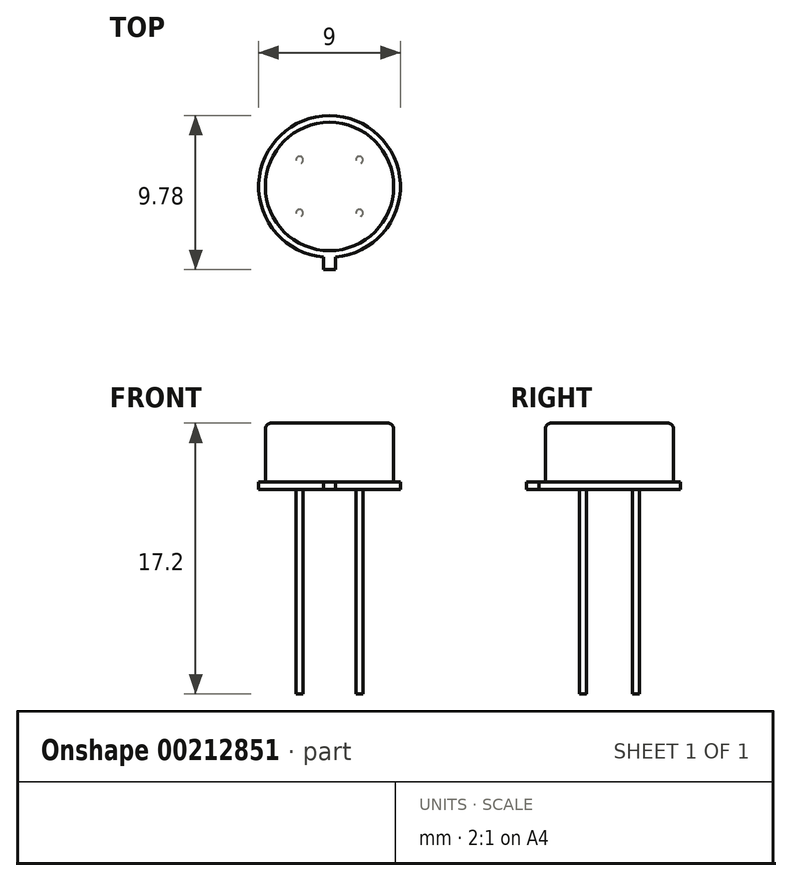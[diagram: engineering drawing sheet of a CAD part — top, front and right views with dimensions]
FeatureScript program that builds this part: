
annotation { "Feature Type Name" : "Feature", "Feature Type Description" : "" }
export const myFeature = defineFeature(function(context is Context, id is Id, definition is map)
    precondition{}
    {
        {
            var Q0;
            Q0=qCreatedBy(makeId("Top.planeOp"),FACE);
            var sketch = newSketch(context, id + "F0", { "sketchPlane" : qUnion([Q0])});
            skCircle(sketch, "E0", {"center": v(0, 0) * mm, "radius": 4.5 * mm});
            skLineSegment(sketch, "E1", {"start": v(-0.37, -4.48) * mm, "end": v(-0.37, -5.28) * mm});
            skLineSegment(sketch, "E2", {"start": v(-0.37, -5.28) * mm, "end": v(0.38, -5.28) * mm});
            skLineSegment(sketch, "E3", {"start": v(0.38, -5.28) * mm, "end": v(0.38, -4.48) * mm});
            skCircle(sketch, "E4", {"center": v(0, 0) * mm, "radius": 2.54 * mm});
            skCircle(sketch, "E5", {"center": v(-1.9, 1.69) * mm, "radius": 0.23 * mm});
            skCircle(sketch, "E6", {"center": v(-1.9, -1.69) * mm, "radius": 0.23 * mm});
            skCircle(sketch, "E7", {"center": v(1.9, -1.69) * mm, "radius": 0.23 * mm});
            skCircle(sketch, "E8", {"center": v(1.9, 1.69) * mm, "radius": 0.23 * mm});
            skCircle(sketch, "E9", {"center": v(0, 0) * mm, "radius": 4.08 * mm});
            skSolve(sketch);
        }
        {
            var Q0;
            Q0=makeQuery(id+"F0.imprint","IMPRINT",FACE,{"disambiguationData":[TD([[makeQuery(id+"F0.imprint","IMPRINT",EDGE,{"derivedFrom":sQuery(id+"F0.wireOp",EDGE,"E9")}),-1.0]])]});
            var Q1;
            {var subQ0=sQuery(id+"F0.wireOp",EDGE,"E1");Q1=makeQuery(id+"F0.imprint","IMPRINT",FACE,{"disambiguationData":[TD([[makeQuery(id+"F0.imprint","IMPRINT",EDGE,{"derivedFrom":subQ0}),1.0]])]});}
            var Q2;
            {var subQ0=sQuery(id+"F0.wireOp",EDGE,"E5");var subQ1=sQuery(id+"F0.wireOp",EDGE,"E4");var subQ2=makeQuery(id+"F0.imprint","INTERSECT",VERTEX,{"disambiguationData":[OD(0.0)],"derivedFrom":[subQ1,subQ0]});Q2=makeQuery(id+"F0.imprint","IMPRINT",FACE,{"disambiguationData":[TD([[makeQuery(id+"F0.imprint","IMPRINT",EDGE,{"disambiguationData":[TD([[subQ2,-1.0]])],"derivedFrom":subQ1}),1.0]])]});}
            var Q3;
            {var subQ0=sQuery(id+"F0.wireOp",EDGE,"E5");var subQ1=sQuery(id+"F0.wireOp",EDGE,"E4");var subQ2=makeQuery(id+"F0.imprint","INTERSECT",VERTEX,{"disambiguationData":[OD(0.0)],"derivedFrom":[subQ1,subQ0]});Q3=makeQuery(id+"F0.imprint","IMPRINT",FACE,{"disambiguationData":[TD([[makeQuery(id+"F0.imprint","IMPRINT",EDGE,{"disambiguationData":[TD([[subQ2,-1.0]])],"derivedFrom":subQ1}),-1.0]])]});}
            var Q4;
            {var subQ0=sQuery(id+"F0.wireOp",EDGE,"E8");var subQ1=sQuery(id+"F0.wireOp",EDGE,"E4");var subQ2=makeQuery(id+"F0.imprint","INTERSECT",VERTEX,{"disambiguationData":[OD(0.0)],"derivedFrom":[subQ1,subQ0]});Q4=makeQuery(id+"F0.imprint","IMPRINT",FACE,{"disambiguationData":[TD([[makeQuery(id+"F0.imprint","IMPRINT",EDGE,{"disambiguationData":[TD([[subQ2,1.0]])],"derivedFrom":subQ1}),-1.0]])]});}
            var Q5;
            {var subQ0=sQuery(id+"F0.wireOp",EDGE,"E8");var subQ1=sQuery(id+"F0.wireOp",EDGE,"E4");var subQ2=makeQuery(id+"F0.imprint","INTERSECT",VERTEX,{"disambiguationData":[OD(0.0)],"derivedFrom":[subQ1,subQ0]});Q5=makeQuery(id+"F0.imprint","IMPRINT",FACE,{"disambiguationData":[TD([[makeQuery(id+"F0.imprint","IMPRINT",EDGE,{"disambiguationData":[TD([[subQ2,1.0]])],"derivedFrom":subQ1}),1.0]])]});}
            var Q6;
            Q6=makeQuery(id+"F0.imprint","IMPRINT",FACE,{"disambiguationData":[TD([[makeQuery(id+"F0.imprint","IMPRINT",EDGE,{"derivedFrom":sQuery(id+"F0.wireOp",EDGE,"E9")}),1.0]])]});
            var Q7;
            {var subQ0=sQuery(id+"F0.wireOp",EDGE,"E7");var subQ1=sQuery(id+"F0.wireOp",EDGE,"E4");var subQ2=makeQuery(id+"F0.imprint","INTERSECT",VERTEX,{"disambiguationData":[OD(0.0)],"derivedFrom":[subQ1,subQ0]});Q7=makeQuery(id+"F0.imprint","IMPRINT",FACE,{"disambiguationData":[TD([[makeQuery(id+"F0.imprint","IMPRINT",EDGE,{"disambiguationData":[TD([[subQ2,-1.0]])],"derivedFrom":subQ1}),1.0]])]});}
            var Q8;
            {var subQ0=sQuery(id+"F0.wireOp",EDGE,"E7");var subQ1=sQuery(id+"F0.wireOp",EDGE,"E4");var subQ2=makeQuery(id+"F0.imprint","INTERSECT",VERTEX,{"disambiguationData":[OD(0.0)],"derivedFrom":[subQ1,subQ0]});Q8=makeQuery(id+"F0.imprint","IMPRINT",FACE,{"disambiguationData":[TD([[makeQuery(id+"F0.imprint","IMPRINT",EDGE,{"disambiguationData":[TD([[subQ2,-1.0]])],"derivedFrom":subQ1}),-1.0]])]});}
            var Q9;
            {var subQ0=sQuery(id+"F0.wireOp",EDGE,"E6");var subQ1=sQuery(id+"F0.wireOp",EDGE,"E4");var subQ2=makeQuery(id+"F0.imprint","INTERSECT",VERTEX,{"disambiguationData":[OD(0.0)],"derivedFrom":[subQ1,subQ0]});Q9=makeQuery(id+"F0.imprint","IMPRINT",FACE,{"disambiguationData":[TD([[makeQuery(id+"F0.imprint","IMPRINT",EDGE,{"disambiguationData":[TD([[subQ2,-1.0]])],"derivedFrom":subQ1}),1.0]])]});}
            var Q10;
            {var subQ0=sQuery(id+"F0.wireOp",EDGE,"E6");var subQ1=sQuery(id+"F0.wireOp",EDGE,"E4");var subQ2=makeQuery(id+"F0.imprint","INTERSECT",VERTEX,{"disambiguationData":[OD(0.0)],"derivedFrom":[subQ1,subQ0]});Q10=makeQuery(id+"F0.imprint","IMPRINT",FACE,{"disambiguationData":[TD([[makeQuery(id+"F0.imprint","IMPRINT",EDGE,{"disambiguationData":[TD([[subQ2,-1.0]])],"derivedFrom":subQ1}),-1.0]])]});}
            var Q11;
            {var subQ0=sQuery(id+"F0.wireOp",EDGE,"E8");var subQ1=sQuery(id+"F0.wireOp",EDGE,"E4");var subQ11=makeQuery(id+"F0.imprint","INTERSECT",VERTEX,{"disambiguationData":[OD(0.0)],"derivedFrom":[subQ1,subQ0]});Q11=makeQuery(id+"F0.imprint","IMPRINT",FACE,{"disambiguationData":[TD([[makeQuery(id+"F0.imprint","IMPRINT",EDGE,{"disambiguationData":[TD([[subQ11,-1.0]])],"derivedFrom":subQ1}),1.0]])]});}
            extrude(context, id + "F1", {"entities" : qUnion([Q0, Q1, Q2, Q3, Q4, Q5, Q6, Q7, Q8, Q9, Q10, Q11]), "depth" : 0.45 * mm});
        }
        {
            var Q0;
            Q0=makeQuery(id+"F0.imprint","IMPRINT",FACE,{"disambiguationData":[TD([[makeQuery(id+"F0.imprint","IMPRINT",EDGE,{"derivedFrom":sQuery(id+"F0.wireOp",EDGE,"E9")}),1.0]])]});
            var Q1;
            {var subQ0=sQuery(id+"F0.wireOp",EDGE,"E8");var subQ1=sQuery(id+"F0.wireOp",EDGE,"E4");var subQ11=makeQuery(id+"F0.imprint","INTERSECT",VERTEX,{"disambiguationData":[OD(0.0)],"derivedFrom":[subQ1,subQ0]});Q1=makeQuery(id+"F0.imprint","IMPRINT",FACE,{"disambiguationData":[TD([[makeQuery(id+"F0.imprint","IMPRINT",EDGE,{"disambiguationData":[TD([[subQ11,-1.0]])],"derivedFrom":subQ1}),1.0]])]});}
            var Q2;
            {var subQ0=sQuery(id+"F0.wireOp",EDGE,"E8");var subQ1=sQuery(id+"F0.wireOp",EDGE,"E4");var subQ2=makeQuery(id+"F0.imprint","INTERSECT",VERTEX,{"disambiguationData":[OD(0.0)],"derivedFrom":[subQ1,subQ0]});Q2=makeQuery(id+"F0.imprint","IMPRINT",FACE,{"disambiguationData":[TD([[makeQuery(id+"F0.imprint","IMPRINT",EDGE,{"disambiguationData":[TD([[subQ2,1.0]])],"derivedFrom":subQ1}),-1.0]])]});}
            var Q3;
            {var subQ0=sQuery(id+"F0.wireOp",EDGE,"E8");var subQ1=sQuery(id+"F0.wireOp",EDGE,"E4");var subQ2=makeQuery(id+"F0.imprint","INTERSECT",VERTEX,{"disambiguationData":[OD(0.0)],"derivedFrom":[subQ1,subQ0]});Q3=makeQuery(id+"F0.imprint","IMPRINT",FACE,{"disambiguationData":[TD([[makeQuery(id+"F0.imprint","IMPRINT",EDGE,{"disambiguationData":[TD([[subQ2,1.0]])],"derivedFrom":subQ1}),1.0]])]});}
            var Q4;
            {var subQ0=sQuery(id+"F0.wireOp",EDGE,"E6");var subQ1=sQuery(id+"F0.wireOp",EDGE,"E4");var subQ2=makeQuery(id+"F0.imprint","INTERSECT",VERTEX,{"disambiguationData":[OD(0.0)],"derivedFrom":[subQ1,subQ0]});Q4=makeQuery(id+"F0.imprint","IMPRINT",FACE,{"disambiguationData":[TD([[makeQuery(id+"F0.imprint","IMPRINT",EDGE,{"disambiguationData":[TD([[subQ2,-1.0]])],"derivedFrom":subQ1}),1.0]])]});}
            var Q5;
            {var subQ0=sQuery(id+"F0.wireOp",EDGE,"E5");var subQ1=sQuery(id+"F0.wireOp",EDGE,"E4");var subQ2=makeQuery(id+"F0.imprint","INTERSECT",VERTEX,{"disambiguationData":[OD(0.0)],"derivedFrom":[subQ1,subQ0]});Q5=makeQuery(id+"F0.imprint","IMPRINT",FACE,{"disambiguationData":[TD([[makeQuery(id+"F0.imprint","IMPRINT",EDGE,{"disambiguationData":[TD([[subQ2,-1.0]])],"derivedFrom":subQ1}),-1.0]])]});}
            var Q6;
            {var subQ0=sQuery(id+"F0.wireOp",EDGE,"E5");var subQ1=sQuery(id+"F0.wireOp",EDGE,"E4");var subQ2=makeQuery(id+"F0.imprint","INTERSECT",VERTEX,{"disambiguationData":[OD(0.0)],"derivedFrom":[subQ1,subQ0]});Q6=makeQuery(id+"F0.imprint","IMPRINT",FACE,{"disambiguationData":[TD([[makeQuery(id+"F0.imprint","IMPRINT",EDGE,{"disambiguationData":[TD([[subQ2,-1.0]])],"derivedFrom":subQ1}),1.0]])]});}
            var Q7;
            {var subQ0=sQuery(id+"F0.wireOp",EDGE,"E7");var subQ1=sQuery(id+"F0.wireOp",EDGE,"E4");var subQ2=makeQuery(id+"F0.imprint","INTERSECT",VERTEX,{"disambiguationData":[OD(0.0)],"derivedFrom":[subQ1,subQ0]});Q7=makeQuery(id+"F0.imprint","IMPRINT",FACE,{"disambiguationData":[TD([[makeQuery(id+"F0.imprint","IMPRINT",EDGE,{"disambiguationData":[TD([[subQ2,-1.0]])],"derivedFrom":subQ1}),-1.0]])]});}
            var Q8;
            {var subQ0=sQuery(id+"F0.wireOp",EDGE,"E7");var subQ1=sQuery(id+"F0.wireOp",EDGE,"E4");var subQ2=makeQuery(id+"F0.imprint","INTERSECT",VERTEX,{"disambiguationData":[OD(0.0)],"derivedFrom":[subQ1,subQ0]});Q8=makeQuery(id+"F0.imprint","IMPRINT",FACE,{"disambiguationData":[TD([[makeQuery(id+"F0.imprint","IMPRINT",EDGE,{"disambiguationData":[TD([[subQ2,-1.0]])],"derivedFrom":subQ1}),1.0]])]});}
            var Q9;
            {var subQ0=sQuery(id+"F0.wireOp",EDGE,"E6");var subQ1=sQuery(id+"F0.wireOp",EDGE,"E4");var subQ2=makeQuery(id+"F0.imprint","INTERSECT",VERTEX,{"disambiguationData":[OD(0.0)],"derivedFrom":[subQ1,subQ0]});Q9=makeQuery(id+"F0.imprint","IMPRINT",FACE,{"disambiguationData":[TD([[makeQuery(id+"F0.imprint","IMPRINT",EDGE,{"disambiguationData":[TD([[subQ2,-1.0]])],"derivedFrom":subQ1}),-1.0]])]});}
            extrude(context, id + "F2", {"entities" : qUnion([Q0, Q1, Q2, Q3, Q4, Q5, Q6, Q7, Q8, Q9]), "operationType" : NewBodyOperationType.ADD, "depth" : 4.2 * mm});
        }
        {
            var Q0;
            {var subQ0=sQuery(id+"F0.wireOp",EDGE,"E8");var subQ1=sQuery(id+"F0.wireOp",EDGE,"E4");var subQ2=makeQuery(id+"F0.imprint","INTERSECT",VERTEX,{"disambiguationData":[OD(0.0)],"derivedFrom":[subQ1,subQ0]});Q0=makeQuery(id+"F0.imprint","IMPRINT",FACE,{"disambiguationData":[TD([[makeQuery(id+"F0.imprint","IMPRINT",EDGE,{"disambiguationData":[TD([[subQ2,1.0]])],"derivedFrom":subQ1}),-1.0]])]});}
            var Q1;
            {var subQ0=sQuery(id+"F0.wireOp",EDGE,"E8");var subQ1=sQuery(id+"F0.wireOp",EDGE,"E4");var subQ2=makeQuery(id+"F0.imprint","INTERSECT",VERTEX,{"disambiguationData":[OD(0.0)],"derivedFrom":[subQ1,subQ0]});Q1=makeQuery(id+"F0.imprint","IMPRINT",FACE,{"disambiguationData":[TD([[makeQuery(id+"F0.imprint","IMPRINT",EDGE,{"disambiguationData":[TD([[subQ2,1.0]])],"derivedFrom":subQ1}),1.0]])]});}
            var Q2;
            {var subQ0=sQuery(id+"F0.wireOp",EDGE,"E7");var subQ1=sQuery(id+"F0.wireOp",EDGE,"E4");var subQ2=makeQuery(id+"F0.imprint","INTERSECT",VERTEX,{"disambiguationData":[OD(0.0)],"derivedFrom":[subQ1,subQ0]});Q2=makeQuery(id+"F0.imprint","IMPRINT",FACE,{"disambiguationData":[TD([[makeQuery(id+"F0.imprint","IMPRINT",EDGE,{"disambiguationData":[TD([[subQ2,-1.0]])],"derivedFrom":subQ1}),-1.0]])]});}
            var Q3;
            {var subQ0=sQuery(id+"F0.wireOp",EDGE,"E7");var subQ1=sQuery(id+"F0.wireOp",EDGE,"E4");var subQ2=makeQuery(id+"F0.imprint","INTERSECT",VERTEX,{"disambiguationData":[OD(0.0)],"derivedFrom":[subQ1,subQ0]});Q3=makeQuery(id+"F0.imprint","IMPRINT",FACE,{"disambiguationData":[TD([[makeQuery(id+"F0.imprint","IMPRINT",EDGE,{"disambiguationData":[TD([[subQ2,-1.0]])],"derivedFrom":subQ1}),1.0]])]});}
            var Q4;
            {var subQ0=sQuery(id+"F0.wireOp",EDGE,"E5");var subQ1=sQuery(id+"F0.wireOp",EDGE,"E4");var subQ2=makeQuery(id+"F0.imprint","INTERSECT",VERTEX,{"disambiguationData":[OD(0.0)],"derivedFrom":[subQ1,subQ0]});Q4=makeQuery(id+"F0.imprint","IMPRINT",FACE,{"disambiguationData":[TD([[makeQuery(id+"F0.imprint","IMPRINT",EDGE,{"disambiguationData":[TD([[subQ2,-1.0]])],"derivedFrom":subQ1}),1.0]])]});}
            var Q5;
            {var subQ0=sQuery(id+"F0.wireOp",EDGE,"E5");var subQ1=sQuery(id+"F0.wireOp",EDGE,"E4");var subQ2=makeQuery(id+"F0.imprint","INTERSECT",VERTEX,{"disambiguationData":[OD(0.0)],"derivedFrom":[subQ1,subQ0]});Q5=makeQuery(id+"F0.imprint","IMPRINT",FACE,{"disambiguationData":[TD([[makeQuery(id+"F0.imprint","IMPRINT",EDGE,{"disambiguationData":[TD([[subQ2,-1.0]])],"derivedFrom":subQ1}),-1.0]])]});}
            var Q6;
            {var subQ0=sQuery(id+"F0.wireOp",EDGE,"E6");var subQ1=sQuery(id+"F0.wireOp",EDGE,"E4");var subQ2=makeQuery(id+"F0.imprint","INTERSECT",VERTEX,{"disambiguationData":[OD(0.0)],"derivedFrom":[subQ1,subQ0]});Q6=makeQuery(id+"F0.imprint","IMPRINT",FACE,{"disambiguationData":[TD([[makeQuery(id+"F0.imprint","IMPRINT",EDGE,{"disambiguationData":[TD([[subQ2,-1.0]])],"derivedFrom":subQ1}),1.0]])]});}
            var Q7;
            {var subQ0=sQuery(id+"F0.wireOp",EDGE,"E6");var subQ1=sQuery(id+"F0.wireOp",EDGE,"E4");var subQ2=makeQuery(id+"F0.imprint","INTERSECT",VERTEX,{"disambiguationData":[OD(0.0)],"derivedFrom":[subQ1,subQ0]});Q7=makeQuery(id+"F0.imprint","IMPRINT",FACE,{"disambiguationData":[TD([[makeQuery(id+"F0.imprint","IMPRINT",EDGE,{"disambiguationData":[TD([[subQ2,-1.0]])],"derivedFrom":subQ1}),-1.0]])]});}
            extrude(context, id + "F3", {"entities" : qUnion([Q0, Q1, Q2, Q3, Q4, Q5, Q6, Q7]), "operationType" : NewBodyOperationType.ADD, "oppositeDirection" : true, "depth" : 13 * mm});
        }
        {
            var Q0;
            Q0=makeQuery(id+"F2.opExtrude","CAP_EDGE",EDGE,{"disambiguationData":[OSD([sQuery(id+"F0.wireOp",EDGE,"E9")])],"isStart":false});
            fillet(context, id + "F4", {"entities" : qUnion([Q0]), "radius" : 0.39 * mm, "tangentPropagation" : true, "allowEdgeOverflow" : false});
        }
    });
